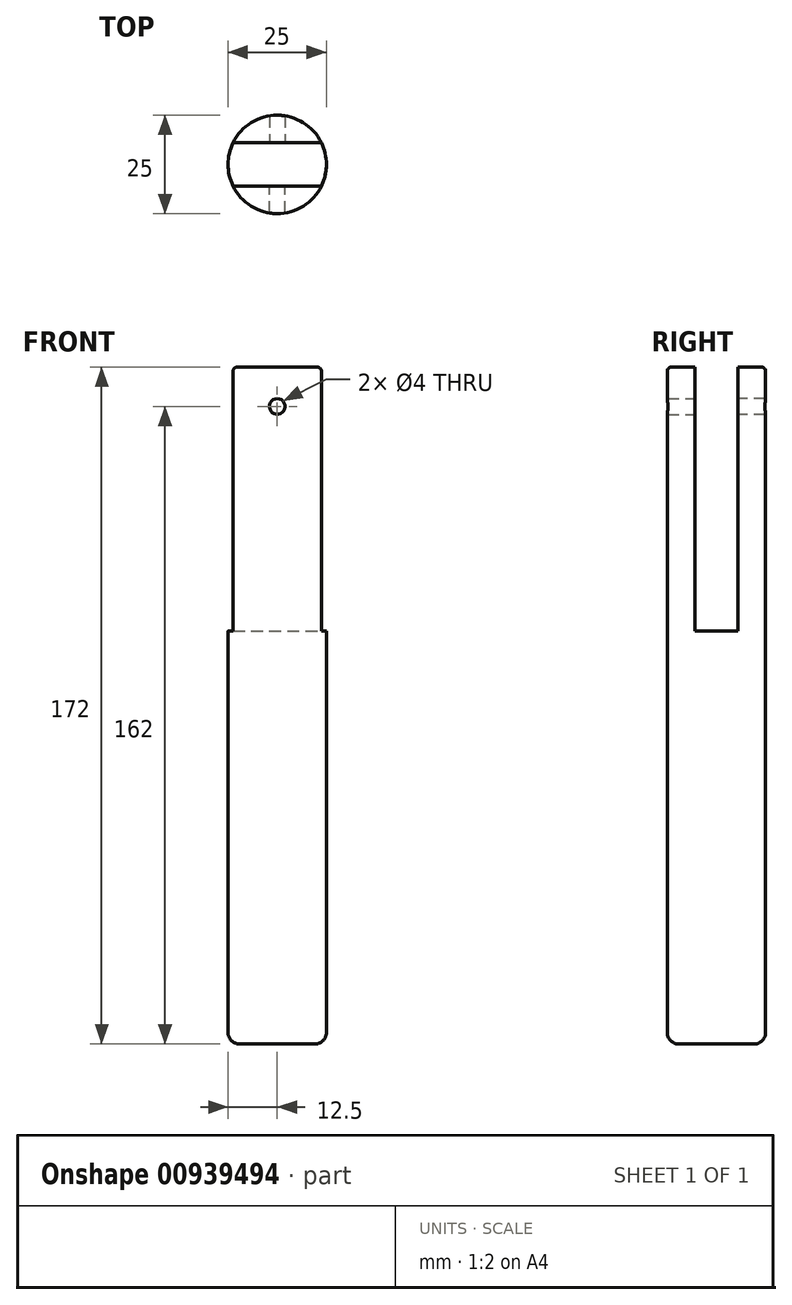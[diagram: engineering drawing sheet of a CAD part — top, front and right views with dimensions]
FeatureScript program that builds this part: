
annotation { "Feature Type Name" : "Feature", "Feature Type Description" : "" }
export const myFeature = defineFeature(function(context is Context, id is Id, definition is map)
    precondition{}
    {
        {
            var Q0;
            Q0=qCreatedBy(makeId("Top.planeOp"),FACE);
            var sketch = newSketch(context, id + "F0", { "sketchPlane" : qUnion([Q0])});
            skCircle(sketch, "E0", {"center": v(0, 0) * mm, "radius": 12.5 * mm});
            skSolve(sketch);
        }
        {
            var Q0;
            Q0 = qSketchRegion(id + "F0", true);
            extrude(context, id + "F1", {"entities" : qUnion([Q0]), "depth" : 105 * mm, "offsetDistance" : 25 * mm});
        }
        {
            var Q0;
            Q0=makeQuery(id+"F1.opExtrude","CAP_FACE",FACE,{"disambiguationData":[OSD([sQuery(id+"F0.wireOp",EDGE,"E0")])],"isStart":false});
            var sketch = newSketch(context, id + "F2", { "sketchPlane" : qUnion([Q0])});
            skLineSegment(sketch, "E1", {"start": v(-11.22, 5.52) * mm, "end": v(11.22, 5.52) * mm});
            skLineSegment(sketch, "E2", {"start": v(-11.23, -5.48) * mm, "end": v(11.23, -5.48) * mm});
            skSolve(sketch);
        }
        {
            var Q0;
            {var subQ0=sQuery(id+"F2.wireOp",EDGE,"E2");Q0=makeQuery(id+"F2.imprint","IMPRINT",FACE,{"disambiguationData":[TD([[makeQuery(id+"F2.imprint","IMPRINT",EDGE,{"derivedFrom":subQ0}),-1.0]])]});}
            var Q1;
            {var subQ0=sQuery(id+"F2.wireOp",EDGE,"E1");Q1=makeQuery(id+"F2.imprint","IMPRINT",FACE,{"disambiguationData":[TD([[makeQuery(id+"F2.imprint","IMPRINT",EDGE,{"derivedFrom":subQ0}),1.0]])]});}
            extrude(context, id + "F3", {"entities" : qUnion([Q0, Q1]), "operationType" : NewBodyOperationType.ADD, "depth" : 67 * mm, "offsetDistance" : 25 * mm});
        }
        {
            var Q0;
            Q0=makeQuery(id+"F1.opExtrude","CAP_EDGE",EDGE,{"disambiguationData":[OSD([sQuery(id+"F0.wireOp",EDGE,"E0")])],"isStart":true});
            fillet(context, id + "F4", {"entities" : qUnion([Q0]), "radius" : 3 * mm, "tangentPropagation" : true, "allowEdgeOverflow" : false});
        }
        {
            var Q0;
            Q0=makeQuery(id+"F3.opExtrude","SWEPT_FACE",FACE,{"disambiguationData":[OSD([sQuery(id+"F2.wireOp",EDGE,"E1")])]});
            var sketch = newSketch(context, id + "F5", { "sketchPlane" : qUnion([Q0])});
            skPoint(sketch, "E3", {"position": v(0, 162) * mm});
            skPoint(sketch, "E3.positionSnap0", {"position": v(0, 172) * mm});
            skSolve(sketch);
        }
        {
            var Q0;
            Q0=sQuery(id+"F5.wireOp",VERTEX,"E3");
            var Q1;
            Q1=makeQuery(id+"F1.opExtrude","SWEPT_BODY",BODY,{"disambiguationData":[OSD([sQuery(id+"F0.wireOp",EDGE,"E0")])]});
            hole(context, id + "F6", {"style" : HoleStyle.SIMPLE, "endStyle" : HoleEndStyle.BLIND, "holeDiameter" : 4 * mm, "majorDiameter" : 5 * mm, "holeDepth" : 20 * mm, "isTappedThrough" : true, "tappedDepth" : 12 * mm, "tapClearance" : 3, "locations" : qUnion([Q0]), "scope" : qUnion([Q1])});
        }
        {
            var Q0;
            Q0=sQuery(id+"F5.wireOp",VERTEX,"E3");
            var Q1;
            Q1=makeQuery(id+"F1.opExtrude","SWEPT_BODY",BODY,{"disambiguationData":[OSD([sQuery(id+"F0.wireOp",EDGE,"E0")])]});
            hole(context, id + "F7", {"style" : HoleStyle.SIMPLE, "endStyle" : HoleEndStyle.BLIND, "oppositeDirection" : true, "holeDiameter" : 4 * mm, "majorDiameter" : 5 * mm, "holeDepth" : 20 * mm, "isTappedThrough" : true, "tappedDepth" : 12 * mm, "tapClearance" : 3, "locations" : qUnion([Q0]), "scope" : qUnion([Q1])});
        }
        {
            var Q0;
            {var subQ0=sQuery(id+"F2.wireOp",EDGE,"E1");var subQ1=sQuery(id+"F0.wireOp",EDGE,"E0");var subQ2=makeQuery(id+"F1.opExtrude","CAP_EDGE",EDGE,{"disambiguationData":[OSD([subQ1])],"isStart":false});Q0=makeQuery(id+"F3.opExtrude","CAP_EDGE",EDGE,{"disambiguationData":[OSD([subQ1]),TDD([makeQuery(id+"F2.imprint","IMPRINT",EDGE,{"disambiguationData":[TD([[makeQuery(id+"F2.imprint","INTERSECT",VERTEX,{"disambiguationData":[OD(0.0)],"derivedFrom":[subQ2,subQ0]}),1.0]])],"derivedFrom":subQ2})])],"isStart":false});}
            var Q1;
            {var subQ0=sQuery(id+"F2.wireOp",EDGE,"E2");var subQ1=sQuery(id+"F0.wireOp",EDGE,"E0");var subQ2=makeQuery(id+"F1.opExtrude","CAP_EDGE",EDGE,{"disambiguationData":[OSD([subQ1])],"isStart":false});Q1=makeQuery(id+"F3.opExtrude","CAP_EDGE",EDGE,{"disambiguationData":[OSD([subQ1]),TDD([makeQuery(id+"F2.imprint","IMPRINT",EDGE,{"disambiguationData":[TD([[makeQuery(id+"F2.imprint","INTERSECT",VERTEX,{"disambiguationData":[OD(0.0)],"derivedFrom":[subQ2,subQ0]}),-1.0]])],"derivedFrom":subQ2})])],"isStart":false});}
            fillet(context, id + "F8", {"entities" : qUnion([Q0, Q1]), "radius" : 1 * mm, "tangentPropagation" : true, "allowEdgeOverflow" : false});
        }
    });
